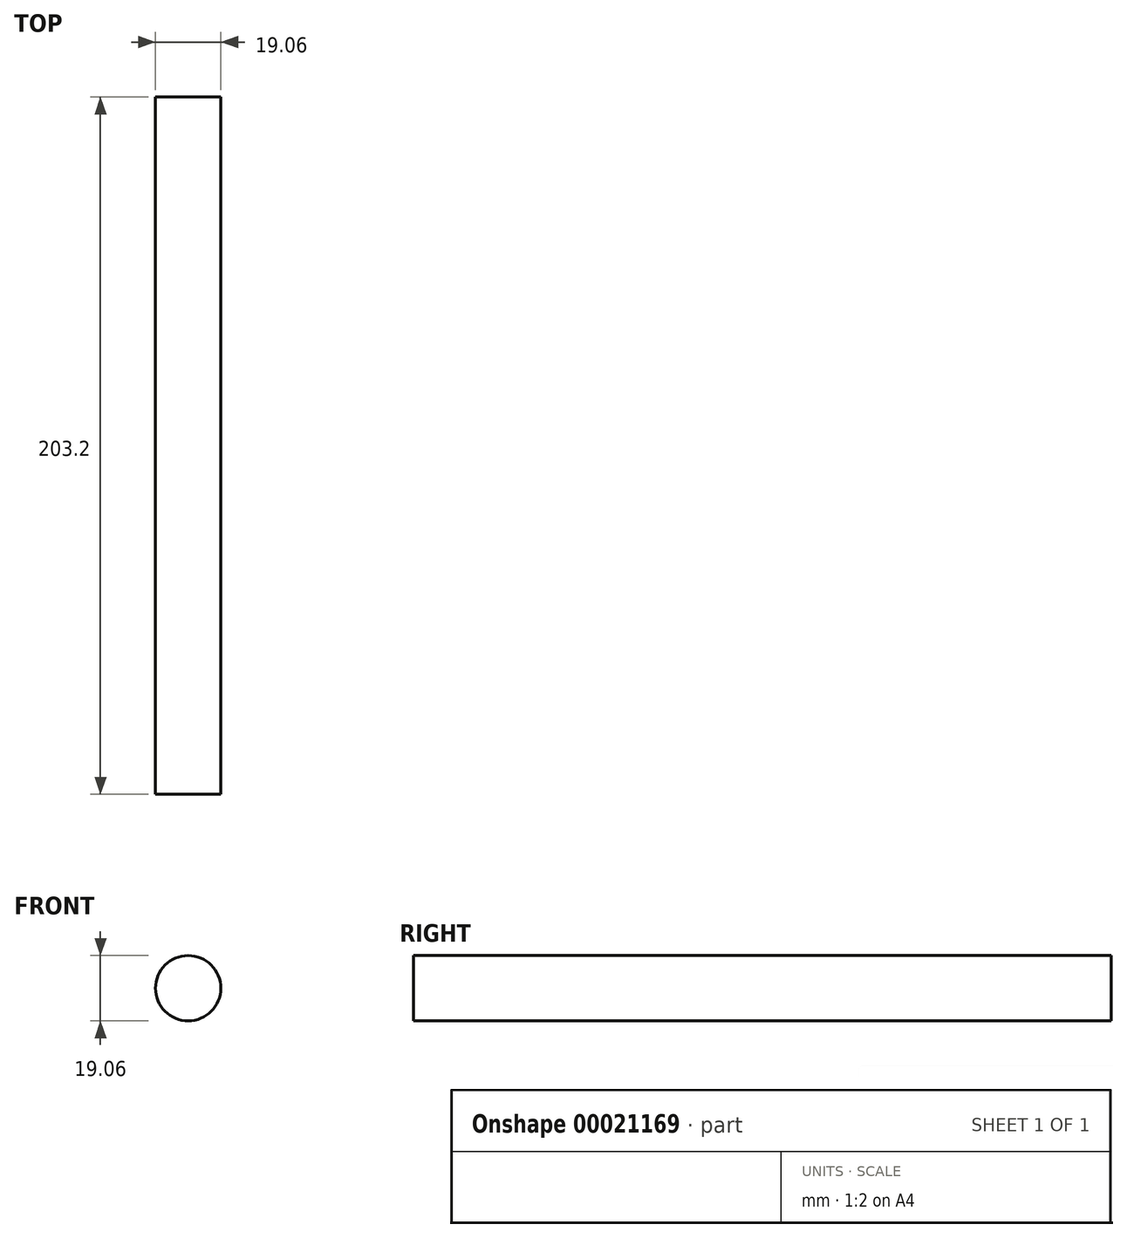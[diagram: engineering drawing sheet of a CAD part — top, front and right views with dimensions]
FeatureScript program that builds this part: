
annotation { "Feature Type Name" : "Feature", "Feature Type Description" : "" }
export const myFeature = defineFeature(function(context is Context, id is Id, definition is map)
    precondition{}
    {
        {
            var Q0;
            Q0=qCreatedBy(makeId("Front.planeOp"),FACE);
            var sketch = newSketch(context, id + "F0", { "sketchPlane" : qUnion([Q0])});
            skCircle(sketch, "E0", {"center": v(0, 0) * mm, "radius": 9.53 * mm});
            skSolve(sketch);
        }
        {
            var Q0;
            Q0=makeQuery(id+"F0.imprint","IMPRINT",FACE,{"disambiguationData":[TD([[makeQuery(id+"F0.imprint","IMPRINT",EDGE,{"derivedFrom":sQuery(id+"F0.wireOp",EDGE,"E0")}),1.0]])]});
            extrude(context, id + "F1", {"entities" : qUnion([Q0]), "depth" : 203.2 * mm});
        }
    });
